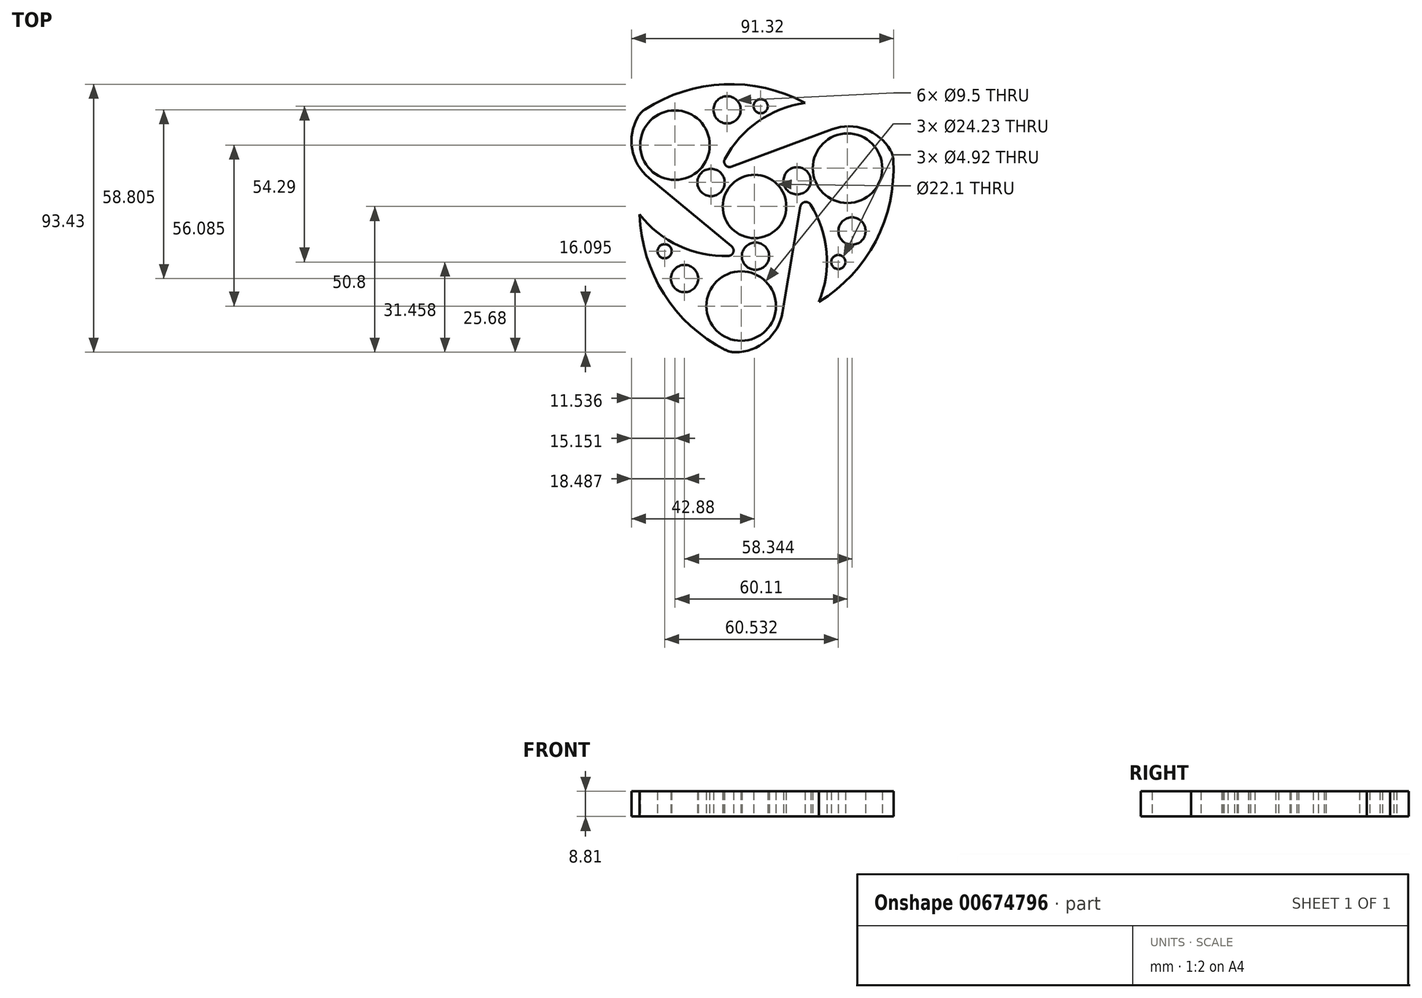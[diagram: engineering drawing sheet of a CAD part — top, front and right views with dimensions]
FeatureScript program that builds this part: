
annotation { "Feature Type Name" : "Feature", "Feature Type Description" : "" }
export const myFeature = defineFeature(function(context is Context, id is Id, definition is map)
    precondition{}
    {
        {
            var Q0;
            Q0=qCreatedBy(makeId("Top.planeOp"),FACE);
            var sketch = newSketch(context, id + "F0", { "sketchPlane" : qUnion([Q0])});
            skCircle(sketch, "E0", {"center": v(0, 0) * mm, "radius": 11.05 * mm});
            skCircle(sketch, "E1", {"center": v(32.38, 13.32) * mm, "radius": 12.12 * mm});
            skArc(sketch, "E2", {"start": v(48.25, 17.76) * mm, "mid": v(39.5, 26.58) * mm, "end": v(27.07, 26.9) * mm});
            skArc(sketch, "E3", {"start": v(22.42, -33.26) * mm, "mid": v(42.55, -11.4) * mm, "end": v(48.25, 17.76) * mm});
            skArc(sketch, "E4", {"start": v(22.42, -33.26) * mm, "mid": v(25.07, -15.93) * mm, "end": v(19.5, 0.7) * mm});
            skArc(sketch, "E5", {"start": v(19.5, 0.7) * mm, "mid": v(17.51, 1.56) * mm, "end": v(16, 0) * mm});
            skLineSegment(sketch, "E6", {"start": v(16, 0) * mm, "end": v(9.76, -36.9) * mm});
            skPoint(sketch, "E7.end.orphan", {"position": v(-12.23, -19.13) * mm});
            skPoint(sketch, "E7.start.orphan", {"position": v(-41.2, -7.33) * mm});
            skPoint(sketch, "E8.end.orphan", {"position": v(-6.54, -14.5) * mm});
            skPoint(sketch, "E9.start.orphan", {"position": v(12.91, 38.24) * mm});
            skPoint(sketch, "E10.start.orphan", {"position": v(-13.07, 14.39) * mm});
            skPoint(sketch, "E11.start.orphan", {"position": v(-10.34, 12.08) * mm});
            skPoint(sketch, "E12.center.orphan", {"position": v(-4.84, -34.68) * mm});
            skPoint(sketch, "E13.center.orphan", {"position": v(-27.73, 21.38) * mm});
            skCircle(sketch, "E14.1.1", {"center": v(-27.73, 21.38) * mm, "radius": 12.12 * mm});
            skArc(sketch, "E14.1.2", {"start": v(-39.5, 32.9) * mm, "mid": v(-42.76, 20.91) * mm, "end": v(-36.83, 10) * mm});
            skArc(sketch, "E14.1.3", {"start": v(17.6, 36.05) * mm, "mid": v(-11.4, 42.55) * mm, "end": v(-39.5, 32.9) * mm});
            skArc(sketch, "E14.1.4", {"start": v(17.6, 36.05) * mm, "mid": v(1.26, 29.67) * mm, "end": v(-10.36, 16.54) * mm});
            skArc(sketch, "E14.1.5", {"start": v(-10.36, 16.54) * mm, "mid": v(-10.1, 14.39) * mm, "end": v(-8, 13.86) * mm});
            skLineSegment(sketch, "E14.1.6", {"start": v(-8, 13.86) * mm, "end": v(27.07, 26.9) * mm});
            skCircle(sketch, "E14.2.0", {"center": v(0, 0) * mm, "radius": 35.01 * mm, "construction": true});
            skCircle(sketch, "E14.2.1", {"center": v(-4.65, -34.7) * mm, "radius": 12.12 * mm});
            skArc(sketch, "E14.2.2", {"start": v(-8.74, -50.67) * mm, "mid": v(3.27, -47.5) * mm, "end": v(9.76, -36.9) * mm});
            skArc(sketch, "E14.2.3", {"start": v(-40.02, -2.8) * mm, "mid": v(-31.15, -31.15) * mm, "end": v(-8.74, -50.67) * mm});
            skArc(sketch, "E14.2.4", {"start": v(-40.02, -2.8) * mm, "mid": v(-26.33, -13.74) * mm, "end": v(-9.15, -17.24) * mm});
            skArc(sketch, "E14.2.5", {"start": v(-9.15, -17.24) * mm, "mid": v(-7.4, -15.95) * mm, "end": v(-8, -13.86) * mm});
            skLineSegment(sketch, "E14.2.6", {"start": v(-8, -13.86) * mm, "end": v(-36.83, 10) * mm});
            skCircle(sketch, "E15", {"center": v(2.16, 34.95) * mm, "radius": 2.46 * mm});
            skCircle(sketch, "E16", {"center": v(-9.56, 33.69) * mm, "radius": 4.75 * mm});
            skCircle(sketch, "E17.1.0", {"center": v(-24.4, -25.12) * mm, "radius": 4.75 * mm});
            skCircle(sketch, "E17.1.1", {"center": v(-31.34, -15.6) * mm, "radius": 2.46 * mm});
            skCircle(sketch, "E17.2.0", {"center": v(33.95, -8.56) * mm, "radius": 4.75 * mm});
            skCircle(sketch, "E17.2.1", {"center": v(29.19, -19.34) * mm, "radius": 2.46 * mm});
            skCircle(sketch, "E18", {"center": v(0.33, -17.32) * mm, "radius": 4.75 * mm});
            skCircle(sketch, "E19", {"center": v(-15.17, 8.37) * mm, "radius": 4.75 * mm});
            skCircle(sketch, "E20", {"center": v(14.83, 8.95) * mm, "radius": 4.75 * mm});
            skLineSegment(sketch, "E21", {"start": v(0, 0) * mm, "end": v(-30.66, 16.92) * mm, "construction": true});
            skLineSegment(sketch, "E22.1.0", {"start": v(0, 0) * mm, "end": v(0.67, -35) * mm, "construction": true});
            skLineSegment(sketch, "E22.2.0", {"start": v(0, 0) * mm, "end": v(29.98, 18.09) * mm, "construction": true});
            skCircle(sketch, "E23", {"center": v(13.47, 115.92) * mm, "radius": 11.05 * mm});
            skCircle(sketch, "E24", {"center": v(45.85, 129.24) * mm, "radius": 12.12 * mm});
            skArc(sketch, "E25", {"start": v(61.72, 133.68) * mm, "mid": v(52.96, 142.5) * mm, "end": v(40.54, 142.81) * mm});
            skArc(sketch, "E26", {"start": v(35.9, 82.66) * mm, "mid": v(56.02, 104.52) * mm, "end": v(61.72, 133.68) * mm});
            skArc(sketch, "E27", {"start": v(35.9, 82.66) * mm, "mid": v(38.53, 99.99) * mm, "end": v(32.97, 116.61) * mm});
            skArc(sketch, "E28", {"start": v(32.97, 116.61) * mm, "mid": v(30.98, 117.47) * mm, "end": v(29.47, 115.92) * mm});
            skLineSegment(sketch, "E29", {"start": v(29.47, 115.92) * mm, "end": v(23.23, 79.02) * mm});
            skPoint(sketch, "E30.end.orphan", {"position": v(1.24, 96.79) * mm});
            skPoint(sketch, "E30.start.orphan", {"position": v(-27.74, 108.59) * mm});
            skPoint(sketch, "E31.end.orphan", {"position": v(6.93, 101.42) * mm});
            skPoint(sketch, "E32.start.orphan", {"position": v(26.38, 154.16) * mm});
            skPoint(sketch, "E33.start.orphan", {"position": v(0.4, 130.3) * mm});
            skPoint(sketch, "E34.start.orphan", {"position": v(3.12, 128) * mm});
            skPoint(sketch, "E35.center.orphan", {"position": v(8.62, 81.24) * mm});
            skPoint(sketch, "E36.center.orphan", {"position": v(-14.26, 137.3) * mm});
            skCircle(sketch, "E37.1.1", {"center": v(-14.26, 137.3) * mm, "radius": 12.12 * mm});
            skArc(sketch, "E37.1.2", {"start": v(-26.04, 148.82) * mm, "mid": v(-29.3, 136.83) * mm, "end": v(-23.36, 125.91) * mm});
            skArc(sketch, "E37.1.3", {"start": v(31.06, 151.97) * mm, "mid": v(2.06, 158.47) * mm, "end": v(-26.04, 148.82) * mm});
            skArc(sketch, "E37.1.4", {"start": v(31.06, 151.97) * mm, "mid": v(14.73, 145.59) * mm, "end": v(3.11, 132.46) * mm});
            skArc(sketch, "E37.1.5", {"start": v(3.11, 132.46) * mm, "mid": v(3.36, 130.3) * mm, "end": v(5.47, 129.77) * mm});
            skLineSegment(sketch, "E37.1.6", {"start": v(5.47, 129.77) * mm, "end": v(40.54, 142.81) * mm});
            skCircle(sketch, "E37.2.0", {"center": v(13.47, 115.92) * mm, "radius": 35.01 * mm, "construction": true});
            skCircle(sketch, "E37.2.1", {"center": v(8.82, 81.21) * mm, "radius": 12.12 * mm});
            skArc(sketch, "E37.2.2", {"start": v(4.72, 65.25) * mm, "mid": v(16.74, 68.42) * mm, "end": v(23.23, 79.02) * mm});
            skArc(sketch, "E37.2.3", {"start": v(-26.55, 113.13) * mm, "mid": v(-17.68, 84.77) * mm, "end": v(4.72, 65.25) * mm});
            skArc(sketch, "E37.2.4", {"start": v(-26.55, 113.13) * mm, "mid": v(-12.86, 102.17) * mm, "end": v(4.32, 98.67) * mm});
            skArc(sketch, "E37.2.5", {"start": v(4.32, 98.67) * mm, "mid": v(6.06, 99.97) * mm, "end": v(5.47, 102.06) * mm});
            skLineSegment(sketch, "E37.2.6", {"start": v(5.47, 102.06) * mm, "end": v(-23.36, 125.91) * mm});
            skCircle(sketch, "E38", {"center": v(15.62, 150.86) * mm, "radius": 2.46 * mm});
            skCircle(sketch, "E39", {"center": v(3.9, 149.6) * mm, "radius": 4.75 * mm});
            skCircle(sketch, "E40.1.0", {"center": v(-10.93, 90.8) * mm, "radius": 4.75 * mm});
            skCircle(sketch, "E40.1.1", {"center": v(-17.88, 100.3) * mm, "radius": 2.46 * mm});
            skCircle(sketch, "E40.2.0", {"center": v(47.42, 107.35) * mm, "radius": 4.75 * mm});
            skCircle(sketch, "E40.2.1", {"center": v(42.66, 96.57) * mm, "radius": 2.46 * mm});
            skCircle(sketch, "E41", {"center": v(13.8, 98.6) * mm, "radius": 4.75 * mm});
            skCircle(sketch, "E42", {"center": v(-1.7, 124.29) * mm, "radius": 4.75 * mm});
            skCircle(sketch, "E43", {"center": v(28.3, 124.86) * mm, "radius": 4.75 * mm});
            skLineSegment(sketch, "E44", {"start": v(13.47, 115.92) * mm, "end": v(-17.19, 132.84) * mm, "construction": true});
            skLineSegment(sketch, "E45.1.0", {"start": v(13.47, 115.92) * mm, "end": v(14.14, 80.9) * mm, "construction": true});
            skLineSegment(sketch, "E45.2.0", {"start": v(13.47, 115.92) * mm, "end": v(43.45, 134) * mm, "construction": true});
            skSolve(sketch);
        }
        {
            var Q0;
            Q0=makeQuery(id+"F0.imprint","IMPRINT",FACE,{"disambiguationData":[TD([[makeQuery(id+"F0.imprint","IMPRINT",EDGE,{"derivedFrom":sQuery(id+"F0.wireOp",EDGE,"E0")}),-1.0]])]});
            extrude(context, id + "F1", {"entities" : qUnion([Q0]), "depth" : 8.8 * mm, "offsetDistance" : 25.4 * mm});
        }
        {
            var Q0;
            Q0=makeQuery(id+"F1.opExtrude","SWEPT_EDGE",EDGE,{"disambiguationData":[OSD([sQuery(id+"F0.wireOp",EDGE,"E14.1.2"),sQuery(id+"F0.wireOp",EDGE,"E14.1.3")])]});
            var Q1;
            Q1=makeQuery(id+"F1.opExtrude","SWEPT_EDGE",EDGE,{"disambiguationData":[OSD([sQuery(id+"F0.wireOp",EDGE,"E2"),sQuery(id+"F0.wireOp",EDGE,"E3")])]});
            var Q2;
            Q2=makeQuery(id+"F1.opExtrude","SWEPT_EDGE",EDGE,{"disambiguationData":[OSD([sQuery(id+"F0.wireOp",EDGE,"E14.2.2"),sQuery(id+"F0.wireOp",EDGE,"E14.2.3")])]});
            fillet(context, id + "F2", {"entities" : qUnion([Q0, Q1, Q2]), "radius" : 7.62 * mm, "tangentPropagation" : true, "allowEdgeOverflow" : false});
        }
    });
